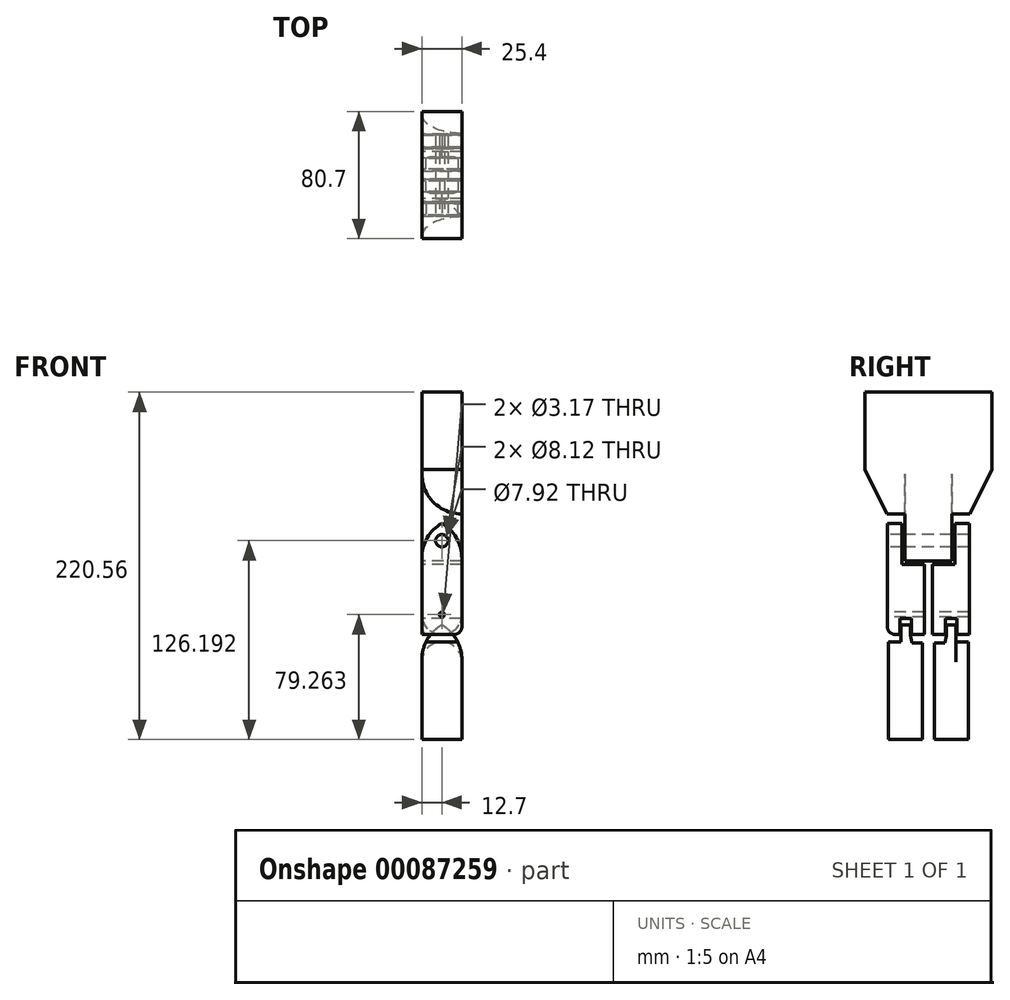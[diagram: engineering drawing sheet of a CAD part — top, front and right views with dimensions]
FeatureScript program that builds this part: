
annotation { "Feature Type Name" : "Feature", "Feature Type Description" : "" }
export const myFeature = defineFeature(function(context is Context, id is Id, definition is map)
    precondition{}
    {
        {
            var Q0;
            Q0=qCreatedBy(makeId("Right.planeOp"),FACE);
            var sketch = newSketch(context, id + "F0", { "sketchPlane" : qUnion([Q0])});
            skLineSegment(sketch, "E0.bottom", {"start": v(36.52, -30.29) * mm, "end": v(-36.52, -30.29) * mm});
            skLineSegment(sketch, "E0.top", {"start": v(36.52, 30.29) * mm, "end": v(-36.52, 30.29) * mm});
            skLineSegment(sketch, "E0.left", {"start": v(36.52, -30.29) * mm, "end": v(36.52, 30.29) * mm});
            skLineSegment(sketch, "E0.right", {"start": v(-36.52, -30.29) * mm, "end": v(-36.52, 30.29) * mm});
            skPoint(sketch, "E0.middle", {"position": v(0, 0) * mm});
            skLineSegment(sketch, "E1.bottom", {"start": v(53.47, 30.29) * mm, "end": v(41.87, 30.29) * mm});
            skLineSegment(sketch, "E1.top", {"start": v(53.47, -12.15) * mm, "end": v(41.87, -12.15) * mm});
            skLineSegment(sketch, "E1.left", {"start": v(53.47, 30.29) * mm, "end": v(53.47, -12.15) * mm});
            skLineSegment(sketch, "E1.right", {"start": v(41.87, 30.29) * mm, "end": v(41.87, -12.15) * mm});
            skLineSegment(sketch, "E2", {"start": v(41.87, 30.29) * mm, "end": v(36.52, 30.29) * mm});
            skLineSegment(sketch, "E3", {"start": v(50.5, -12.15) * mm, "end": v(50.5, 0) * mm});
            skLineSegment(sketch, "E4", {"start": v(50.5, 0) * mm, "end": v(47.23, 0) * mm});
            skLineSegment(sketch, "E5", {"start": v(47.23, 0) * mm, "end": v(47.23, -12.15) * mm});
            skLineSegment(sketch, "E6.bottom", {"start": v(53.47, -16.9) * mm, "end": v(43.06, -16.9) * mm});
            skLineSegment(sketch, "E6.top", {"start": v(53.47, -46.35) * mm, "end": v(43.06, -46.35) * mm});
            skLineSegment(sketch, "E6.left", {"start": v(53.47, -16.9) * mm, "end": v(53.47, -46.35) * mm});
            skLineSegment(sketch, "E6.right", {"start": v(43.06, -16.9) * mm, "end": v(43.06, -46.35) * mm});
            skLineSegment(sketch, "E7", {"start": v(47.23, -12.15) * mm, "end": v(47.23, -16.9) * mm});
            skLineSegment(sketch, "E8", {"start": v(50.5, -12.15) * mm, "end": v(50.5, -16.9) * mm});
            skLineSegment(sketch, "E9.MirrorCS", {"start": v(-53.47, 30.29) * mm, "end": v(-53.47, -12.15) * mm});
            skLineSegment(sketch, "E10.MirrorCS", {"start": v(-53.47, 30.29) * mm, "end": v(-41.87, 30.29) * mm});
            skLineSegment(sketch, "E11.MirrorCS", {"start": v(-41.87, 30.29) * mm, "end": v(-41.87, -12.15) * mm});
            skLineSegment(sketch, "E12.MirrorCS", {"start": v(-41.87, 30.29) * mm, "end": v(-36.52, 30.29) * mm});
            skLineSegment(sketch, "E13.MirrorCS", {"start": v(-47.23, 0) * mm, "end": v(-47.23, -12.15) * mm});
            skLineSegment(sketch, "E14.MirrorCS", {"start": v(-50.5, -12.15) * mm, "end": v(-50.5, 0) * mm});
            skLineSegment(sketch, "E15.MirrorCS", {"start": v(-50.5, 0) * mm, "end": v(-47.23, 0) * mm});
            skLineSegment(sketch, "E16.MirrorCS", {"start": v(-53.47, -12.15) * mm, "end": v(-41.87, -12.15) * mm});
            skLineSegment(sketch, "E17.MirrorCS", {"start": v(-53.47, -16.9) * mm, "end": v(-53.47, -46.35) * mm});
            skLineSegment(sketch, "E18.MirrorCS", {"start": v(-53.47, -46.35) * mm, "end": v(-43.06, -46.35) * mm});
            skLineSegment(sketch, "E19.MirrorCS", {"start": v(-43.06, -16.9) * mm, "end": v(-43.06, -46.35) * mm});
            skLineSegment(sketch, "E20.MirrorCS", {"start": v(-53.47, -16.9) * mm, "end": v(-43.06, -16.9) * mm});
            skLineSegment(sketch, "E21.MirrorCS", {"start": v(-50.5, -12.15) * mm, "end": v(-50.5, -16.9) * mm});
            skLineSegment(sketch, "E22.MirrorCS", {"start": v(-47.23, -12.15) * mm, "end": v(-47.23, -16.9) * mm});
            skLineSegment(sketch, "E23", {"start": v(36.52, -30.29) * mm, "end": v(36.52, -138.55) * mm});
            skLineSegment(sketch, "E24", {"start": v(36.52, -138.55) * mm, "end": v(11.43, -138.55) * mm});
            skLineSegment(sketch, "E25", {"start": v(11.43, -138.55) * mm, "end": v(0, -101.39) * mm});
            skLineSegment(sketch, "E26.MirrorCS", {"start": v(-36.52, -30.29) * mm, "end": v(-36.52, -138.55) * mm});
            skLineSegment(sketch, "E27.MirrorCS", {"start": v(-36.52, -138.55) * mm, "end": v(-11.43, -138.55) * mm});
            skLineSegment(sketch, "E28.MirrorCS", {"start": v(-11.43, -138.55) * mm, "end": v(0, -101.39) * mm});
            skLineSegment(sketch, "E29.bottom", {"start": v(33.33, -138.55) * mm, "end": v(14.77, -138.55) * mm});
            skLineSegment(sketch, "E29.top", {"start": v(33.33, -149.5) * mm, "end": v(14.77, -149.5) * mm});
            skLineSegment(sketch, "E29.left", {"start": v(33.33, -138.55) * mm, "end": v(33.33, -149.5) * mm});
            skLineSegment(sketch, "E29.right", {"start": v(14.77, -138.55) * mm, "end": v(14.77, -149.5) * mm});
            skLineSegment(sketch, "E30.MirrorCS", {"start": v(-33.33, -138.55) * mm, "end": v(-33.33, -149.5) * mm});
            skLineSegment(sketch, "E31.MirrorCS", {"start": v(-33.33, -149.5) * mm, "end": v(-14.77, -149.5) * mm});
            skLineSegment(sketch, "E32.MirrorCS", {"start": v(-14.77, -138.55) * mm, "end": v(-14.77, -149.5) * mm});
            skLineSegment(sketch, "E33", {"start": v(89.5, -41.61) * mm, "end": v(-88.4, -41.61) * mm});
            skLineSegment(sketch, "E34", {"start": v(89.9, -37.91) * mm, "end": v(-88.4, -37.91) * mm});
            skArc(sketch, "E35", {"start": v(-88.4, -37.91) * mm, "mid": v(-90.24, -39.76) * mm, "end": v(-88.4, -41.61) * mm});
            skArc(sketch, "E36", {"start": v(89.5, -41.61) * mm, "mid": v(91.36, -39.95) * mm, "end": v(89.9, -37.91) * mm});
            skArc(sketch, "E37", {"start": v(-16.6, 47.3) * mm, "mid": v(1.72, 29.89) * mm, "end": v(20.04, 47.3) * mm, "construction": true});
            skLineSegment(sketch, "E38", {"start": v(-16.6, 47.3) * mm, "end": v(20.04, 47.3) * mm, "construction": true});
            skSolve(sketch);
        }
        {
            var Q0;
            Q0=qCreatedBy(makeId("Right.planeOp"),FACE);
            var sketch = newSketch(context, id + "F1", { "sketchPlane" : qUnion([Q0])});
            skLineSegment(sketch, "E39.0", {"start": v(-16.6, 47.3) * mm, "end": v(20.04, 47.3) * mm});
            skArc(sketch, "E39.1", {"start": v(-16.6, 47.3) * mm, "mid": v(1.72, 29.89) * mm, "end": v(20.04, 47.3) * mm});
            skSolve(sketch);
        }
        {
            var Q0;
            Q0=sQuery(id+"F1.wireOp",EDGE,"E39.1");
            var Q1;
            Q1=sQuery(id+"F1.wireOp",EDGE,"E39.0");
            revolve(context, id + "F2", {"bodyType" : ToolBodyType.SURFACE, "surfaceEntities" : qUnion([Q0]), "axis" : qUnion([Q1]), "revolveType" : RevolveType.FULL});
        }
        {
            var Q0;
            Q0=qCreatedBy(makeId("Right.planeOp"),FACE);
            var sketch = newSketch(context, id + "F3", { "sketchPlane" : qUnion([Q0])});
            skLineSegment(sketch, "E40", {"start": v(-40.35, 30.36) * mm, "end": v(-40.35, 0) * mm});
            skLineSegment(sketch, "E41", {"start": v(-40.35, 0) * mm, "end": v(-40.35, -18.8) * mm});
            skLineSegment(sketch, "E42", {"start": v(-40.35, -18.8) * mm, "end": v(-26.44, -47.09) * mm});
            skLineSegment(sketch, "E43", {"start": v(-26.44, -47.09) * mm, "end": v(-14.84, -47.09) * mm});
            skLineSegment(sketch, "E44", {"start": v(-14.84, -47.09) * mm, "end": v(-14.84, -76.78) * mm});
            skLineSegment(sketch, "E45.MirrorCS", {"start": v(40.35, 30.36) * mm, "end": v(40.35, 0) * mm});
            skLineSegment(sketch, "E46.MirrorCS", {"start": v(40.35, 0) * mm, "end": v(40.35, -18.8) * mm});
            skLineSegment(sketch, "E47.MirrorCS", {"start": v(40.35, -18.8) * mm, "end": v(26.44, -47.09) * mm});
            skLineSegment(sketch, "E48.MirrorCS", {"start": v(26.44, -47.09) * mm, "end": v(14.84, -47.09) * mm});
            skLineSegment(sketch, "E49.MirrorCS", {"start": v(14.84, -47.09) * mm, "end": v(14.84, -76.78) * mm});
            skLineSegment(sketch, "E50", {"start": v(-14.84, -76.78) * mm, "end": v(14.84, -76.78) * mm});
            skLineSegment(sketch, "E51", {"start": v(-40.35, 30.36) * mm, "end": v(40.35, 30.36) * mm});
            skSolve(sketch);
        }
        {
            var Q0;
            Q0=qCreatedBy(makeId("Right.planeOp"),FACE);
            var sketch = newSketch(context, id + "F4", { "sketchPlane" : qUnion([Q0])});
            skLineSegment(sketch, "E52", {"start": v(26.06, -49.53) * mm, "end": v(16.76, -49.53) * mm});
            skLineSegment(sketch, "E53", {"start": v(16.76, -49.53) * mm, "end": v(16.76, -79.23) * mm});
            skLineSegment(sketch, "E54", {"start": v(16.76, -79.23) * mm, "end": v(2.66, -79.23) * mm});
            skLineSegment(sketch, "E55", {"start": v(26.06, -49.53) * mm, "end": v(26.06, -123.64) * mm});
            skLineSegment(sketch, "E56", {"start": v(26.06, -123.64) * mm, "end": v(17.96, -123.64) * mm});
            skLineSegment(sketch, "E57", {"start": v(17.96, -123.64) * mm, "end": v(17.96, -113.44) * mm});
            skLineSegment(sketch, "E58", {"start": v(18.26, -113.44) * mm, "end": v(10.76, -113.44) * mm});
            skLineSegment(sketch, "E59", {"start": v(10.76, -113.44) * mm, "end": v(10.76, -123.64) * mm});
            skLineSegment(sketch, "E60", {"start": v(10.76, -123.64) * mm, "end": v(2.66, -123.64) * mm});
            skLineSegment(sketch, "E61", {"start": v(2.66, -123.64) * mm, "end": v(2.66, -79.23) * mm});
            skLineSegment(sketch, "E62.MirrorCS", {"start": v(-26.06, -49.53) * mm, "end": v(-26.06, -123.64) * mm});
            skLineSegment(sketch, "E63.MirrorCS", {"start": v(-2.66, -123.64) * mm, "end": v(-2.66, -79.23) * mm});
            skLineSegment(sketch, "E64.MirrorCS", {"start": v(-16.76, -79.23) * mm, "end": v(-2.66, -79.23) * mm});
            skLineSegment(sketch, "E65.MirrorCS", {"start": v(-18.26, -113.44) * mm, "end": v(-10.76, -113.44) * mm});
            skLineSegment(sketch, "E66.MirrorCS", {"start": v(-10.76, -123.64) * mm, "end": v(-2.66, -123.64) * mm});
            skLineSegment(sketch, "E67.MirrorCS", {"start": v(-26.06, -123.64) * mm, "end": v(-17.96, -123.64) * mm});
            skLineSegment(sketch, "E68.MirrorCS", {"start": v(-17.96, -123.64) * mm, "end": v(-17.96, -113.44) * mm});
            skLineSegment(sketch, "E69.MirrorCS", {"start": v(-10.76, -113.44) * mm, "end": v(-10.76, -123.64) * mm});
            skLineSegment(sketch, "E70.MirrorCS", {"start": v(-16.76, -49.53) * mm, "end": v(-16.76, -79.23) * mm});
            skLineSegment(sketch, "E71.MirrorCS", {"start": v(-26.06, -49.53) * mm, "end": v(-16.76, -49.53) * mm});
            skSolve(sketch);
        }
        {
            var Q0;
            Q0=qCreatedBy(makeId("Right.planeOp"),FACE);
            var sketch = newSketch(context, id + "F5", { "sketchPlane" : qUnion([Q0])});
            skLineSegment(sketch, "E72", {"start": v(17.38, -114.1) * mm, "end": v(11.5, -114.1) * mm});
            skLineSegment(sketch, "E73", {"start": v(11.5, -114.1) * mm, "end": v(11.5, -123.93) * mm});
            skLineSegment(sketch, "E74", {"start": v(17.38, -114.1) * mm, "end": v(17.38, -124.07) * mm});
            skLineSegment(sketch, "E75", {"start": v(17.38, -124.07) * mm, "end": v(17.38, -128.34) * mm});
            skLineSegment(sketch, "E76", {"start": v(17.38, -128.34) * mm, "end": v(25.3, -128.34) * mm});
            skLineSegment(sketch, "E77", {"start": v(25.3, -128.34) * mm, "end": v(25.3, -190.2) * mm});
            skLineSegment(sketch, "E78", {"start": v(25.3, -190.2) * mm, "end": v(20.45, -190.2) * mm});
            skLineSegment(sketch, "E79", {"start": v(20.45, -190.2) * mm, "end": v(8.22, -190.2) * mm});
            skLineSegment(sketch, "E80", {"start": v(8.22, -190.2) * mm, "end": v(3.86, -190.2) * mm});
            skLineSegment(sketch, "E81", {"start": v(3.86, -190.2) * mm, "end": v(3.86, -129.06) * mm});
            skLineSegment(sketch, "E82", {"start": v(3.86, -129.06) * mm, "end": v(10.4, -129.06) * mm});
            skLineSegment(sketch, "E83", {"start": v(10.4, -129.06) * mm, "end": v(11.5, -123.93) * mm});
            skLineSegment(sketch, "E84.MirrorCS", {"start": v(-25.3, -128.34) * mm, "end": v(-25.3, -190.2) * mm});
            skLineSegment(sketch, "E85.MirrorCS", {"start": v(-17.38, -128.34) * mm, "end": v(-25.3, -128.34) * mm});
            skLineSegment(sketch, "E86.MirrorCS", {"start": v(-3.86, -129.06) * mm, "end": v(-10.4, -129.06) * mm});
            skLineSegment(sketch, "E87.MirrorCS", {"start": v(-3.86, -190.2) * mm, "end": v(-3.86, -129.06) * mm});
            skLineSegment(sketch, "E88.MirrorCS", {"start": v(-25.3, -190.2) * mm, "end": v(-20.45, -190.2) * mm});
            skLineSegment(sketch, "E89.MirrorCS", {"start": v(-20.45, -190.2) * mm, "end": v(-8.22, -190.2) * mm});
            skLineSegment(sketch, "E90.MirrorCS", {"start": v(-8.22, -190.2) * mm, "end": v(-3.86, -190.2) * mm});
            skLineSegment(sketch, "E91.MirrorCS", {"start": v(-10.4, -129.06) * mm, "end": v(-11.5, -123.93) * mm});
            skLineSegment(sketch, "E92.MirrorCS", {"start": v(-17.38, -124.07) * mm, "end": v(-17.38, -128.34) * mm});
            skLineSegment(sketch, "E93.MirrorCS", {"start": v(-11.5, -114.1) * mm, "end": v(-11.5, -123.93) * mm});
            skLineSegment(sketch, "E94.MirrorCS", {"start": v(-17.38, -114.1) * mm, "end": v(-17.38, -124.07) * mm});
            skLineSegment(sketch, "E95.MirrorCS", {"start": v(-17.38, -114.1) * mm, "end": v(-11.5, -114.1) * mm});
            skSolve(sketch);
        }
        {
            var Q0;
            Q0 = qSketchRegion(id + "F5", true);
            extrude(context, id + "F6", {"entities" : qUnion([Q0]), "endBound" : BoundingType.SYMMETRIC, "depth" : 25.4 * mm});
        }
        {
            var Q0;
            Q0 = qSketchRegion(id + "F4", true);
            extrude(context, id + "F7", {"entities" : qUnion([Q0]), "endBound" : BoundingType.SYMMETRIC, "depth" : 25.4 * mm});
        }
        {
            var Q0;
            Q0=makeQuery(id+"F3.imprint","IMPRINT",FACE,{"disambiguationData":[TD([[makeQuery(id+"F3.imprint","IMPRINT",EDGE,{"derivedFrom":sQuery(id+"F3.wireOp",EDGE,"E40")}),1.0]])]});
            extrude(context, id + "F8", {"entities" : qUnion([Q0]), "endBound" : BoundingType.SYMMETRIC, "depth" : 25.4 * mm});
        }
        {
            var Q0;
            Q0=makeQuery(id+"F6.opExtrude","CAP_EDGE",EDGE,{"disambiguationData":[OSD([sQuery(id+"F5.wireOp",EDGE,"E76")])],"isStart":false});
            var Q1;
            Q1=makeQuery(id+"F7.opExtrude","CAP_EDGE",EDGE,{"disambiguationData":[OSD([sQuery(id+"F4.wireOp",EDGE,"E56")])],"isStart":false});
            var Q2;
            Q2=makeQuery(id+"F7.opExtrude","CAP_EDGE",EDGE,{"disambiguationData":[OSD([sQuery(id+"F4.wireOp",EDGE,"E56")])],"isStart":true});
            var Q3;
            Q3=makeQuery(id+"F6.opExtrude","CAP_EDGE",EDGE,{"disambiguationData":[OSD([sQuery(id+"F5.wireOp",EDGE,"E76")])],"isStart":true});
            fillet(context, id + "F9", {"entities" : qUnion([Q0, Q1, Q2, Q3]), "radius" : 12.7 * mm, "tangentPropagation" : true, "allowEdgeOverflow" : false});
        }
        {
            var Q0;
            Q0=makeQuery(id+"F7.opExtrude","CAP_EDGE",EDGE,{"disambiguationData":[OSD([sQuery(id+"F4.wireOp",EDGE,"E67.MirrorCS")])],"isStart":false});
            var Q1;
            Q1=makeQuery(id+"F7.opExtrude","SWEPT_EDGE",EDGE,{"disambiguationData":[OSD([sQuery(id+"F4.wireOp",EDGE,"E62.MirrorCS"),sQuery(id+"F4.wireOp",EDGE,"E67.MirrorCS")])]});
            var Q2;
            Q2=makeQuery(id+"F7.opExtrude","CAP_EDGE",EDGE,{"disambiguationData":[OSD([sQuery(id+"F4.wireOp",EDGE,"E66.MirrorCS")])],"isStart":true});
            var Q3;
            Q3=makeQuery(id+"F7.opExtrude","CAP_EDGE",EDGE,{"disambiguationData":[OSD([sQuery(id+"F4.wireOp",EDGE,"E66.MirrorCS")])],"isStart":false});
            fillet(context, id + "F10", {"entities" : qUnion([Q0, Q1, Q2, Q3]), "radius" : 5.08 * mm, "tangentPropagation" : true, "allowEdgeOverflow" : false});
        }
        {
            var Q0;
            Q0=makeQuery(id+"F6.opExtrude","CAP_EDGE",EDGE,{"disambiguationData":[OSD([sQuery(id+"F5.wireOp",EDGE,"E72")])],"isStart":false});
            var Q1;
            Q1=makeQuery(id+"F6.opExtrude","CAP_EDGE",EDGE,{"disambiguationData":[OSD([sQuery(id+"F5.wireOp",EDGE,"E95.MirrorCS")])],"isStart":false});
            var Q2;
            Q2=makeQuery(id+"F6.opExtrude","CAP_EDGE",EDGE,{"disambiguationData":[OSD([sQuery(id+"F5.wireOp",EDGE,"E95.MirrorCS")])],"isStart":true});
            var Q3;
            Q3=makeQuery(id+"F6.opExtrude","CAP_EDGE",EDGE,{"disambiguationData":[OSD([sQuery(id+"F5.wireOp",EDGE,"E72")])],"isStart":true});
            fillet(context, id + "F11", {"entities" : qUnion([Q0, Q1, Q2, Q3]), "radius" : 25.4 * mm, "tangentPropagation" : true, "allowEdgeOverflow" : false});
        }
        {
            var Q0;
            Q0=makeQuery(id+"F7.opExtrude","CAP_EDGE",EDGE,{"disambiguationData":[OSD([sQuery(id+"F4.wireOp",EDGE,"E52")])],"isStart":true});
            var Q1;
            Q1=makeQuery(id+"F8.opExtrude","CAP_EDGE",EDGE,{"disambiguationData":[OSD([sQuery(id+"F3.wireOp",EDGE,"E48.MirrorCS")])],"isStart":true});
            var Q2;
            Q2=makeQuery(id+"F7.opExtrude","CAP_EDGE",EDGE,{"disambiguationData":[OSD([sQuery(id+"F4.wireOp",EDGE,"E71.MirrorCS")])],"isStart":true});
            var Q3;
            Q3=makeQuery(id+"F7.opExtrude","CAP_EDGE",EDGE,{"disambiguationData":[OSD([sQuery(id+"F4.wireOp",EDGE,"E52")])],"isStart":false});
            var Q4;
            Q4=makeQuery(id+"F7.opExtrude","CAP_EDGE",EDGE,{"disambiguationData":[OSD([sQuery(id+"F4.wireOp",EDGE,"E71.MirrorCS")])],"isStart":false});
            var Q5;
            Q5=makeQuery(id+"F8.opExtrude","CAP_EDGE",EDGE,{"disambiguationData":[OSD([sQuery(id+"F3.wireOp",EDGE,"E43")])],"isStart":true});
            fillet(context, id + "F12", {"entities" : qUnion([Q0, Q1, Q2, Q3, Q4, Q5]), "radius" : 25.4 * mm, "tangentPropagation" : true, "allowEdgeOverflow" : false});
        }
        {
            var Q0;
            Q0=qCreatedBy(makeId("Front.planeOp"),FACE);
            var sketch = newSketch(context, id + "F13", { "sketchPlane" : qUnion([Q0])});
            skCircle(sketch, "E96", {"center": v(0, -63.45) * mm, "radius": 3.2 * mm});
            skSolve(sketch);
        }
        {
            var Q0;
            Q0 = qSketchRegion(id + "F13", true);
            extrude(context, id + "F14", {"entities" : qUnion([Q0]), "operationType" : NewBodyOperationType.REMOVE, "endBound" : BoundingType.THROUGH_ALL, "oppositeDirection" : true, "depth" : 25.4 * mm});
        }
        {
            var Q0;
            Q0=makeQuery(id+"F7.opExtrude","SWEPT_FACE",FACE,{"disambiguationData":[OSD([sQuery(id+"F4.wireOp",EDGE,"E62.MirrorCS")])]});
            var sketch = newSketch(context, id + "F15", { "sketchPlane" : qUnion([Q0])});
            skCircle(sketch, "E97", {"center": v(0, -64) * mm, "radius": 3.96 * mm});
            skSolve(sketch);
        }
        {
            var Q0;
            Q0=makeQuery(id+"F15.imprint","IMPRINT",FACE,{"disambiguationData":[TD([[makeQuery(id+"F15.imprint","IMPRINT",EDGE,{"derivedFrom":sQuery(id+"F15.wireOp",EDGE,"E97")}),1.0]])]});
            extrude(context, id + "F16", {"entities" : qUnion([Q0]), "operationType" : NewBodyOperationType.REMOVE, "endBound" : BoundingType.THROUGH_ALL, "oppositeDirection" : true, "depth" : 25.4 * mm});
        }
        {
            var Q0;
            Q0=makeQuery(id+"F8.opExtrude","SWEPT_FACE",FACE,{"disambiguationData":[OSD([sQuery(id+"F3.wireOp",EDGE,"E44")])]});
            var sketch = newSketch(context, id + "F17", { "sketchPlane" : qUnion([Q0])});
            skCircle(sketch, "E98", {"center": v(0, -64) * mm, "radius": 4.06 * mm});
            skSolve(sketch);
        }
        {
            var Q0;
            Q0=makeQuery(id+"F17.imprint","IMPRINT",FACE,{"disambiguationData":[TD([[makeQuery(id+"F17.imprint","IMPRINT",EDGE,{"derivedFrom":sQuery(id+"F17.wireOp",EDGE,"E98")}),1.0]])]});
            extrude(context, id + "F18", {"entities" : qUnion([Q0]), "operationType" : NewBodyOperationType.REMOVE, "endBound" : BoundingType.THROUGH_ALL, "oppositeDirection" : true, "depth" : 25.4 * mm});
        }
        {
            var Q0;
            Q0=makeQuery(id+"F7.opExtrude","SWEPT_FACE",FACE,{"disambiguationData":[OSD([sQuery(id+"F4.wireOp",EDGE,"E62.MirrorCS")])]});
            var sketch = newSketch(context, id + "F19", { "sketchPlane" : qUnion([Q0])});
            skCircle(sketch, "E99", {"center": v(0, -110.94) * mm, "radius": 1.59 * mm});
            skSolve(sketch);
        }
        {
            var Q0;
            Q0=makeQuery(id+"F19.imprint","IMPRINT",FACE,{"disambiguationData":[TD([[makeQuery(id+"F19.imprint","IMPRINT",EDGE,{"derivedFrom":sQuery(id+"F19.wireOp",EDGE,"E99")}),1.0]])]});
            extrude(context, id + "F20", {"entities" : qUnion([Q0]), "operationType" : NewBodyOperationType.REMOVE, "endBound" : BoundingType.THROUGH_ALL, "oppositeDirection" : true, "depth" : 25.4 * mm});
        }
    });
